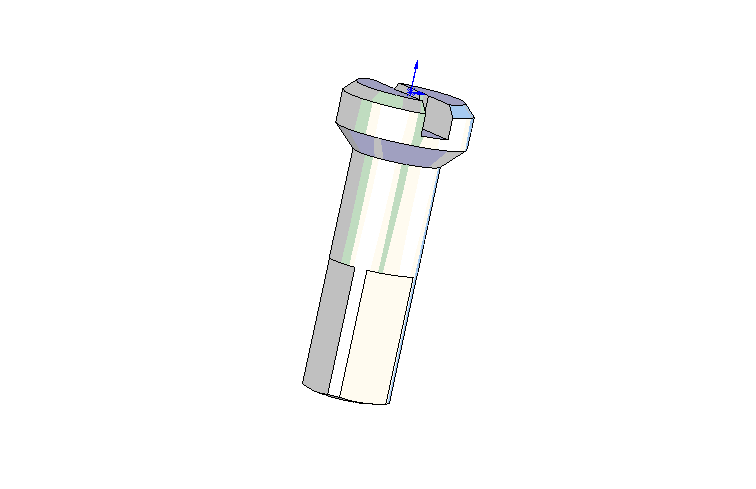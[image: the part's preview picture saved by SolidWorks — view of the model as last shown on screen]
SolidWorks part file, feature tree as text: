
SOLIDWORKS PART (.sldprt)
format: sldprt  version: not decoded by parser v0  size: 207,872 bytes
history: native  units: mm
features: plane x3, sketch x3, cut_extrude x2, material x1, revolve x1, chamfer x1 (+10 scaffold rows collapsed)
feature tree (21):
  scaffold x10  (default folders/planes/origin — collapsed)
  material  "Matériau <non spécifié>"
  plane  "Plan de face"
  plane  "Plan de dessus"
  plane  "Plan de droite"
  sketch  "Esquisse2"  dims[c1.D9=15.0mm c1.D1=1.6mm c1.D2=2.4mm c1.D3=6.0mm c1.D4=14.0mm c1.D5=2.0mm c1.D6=3.0mm c1.D7=6.0mm c1.D8=4.0mm c2.D3=6.0mm c2.D4=14.0mm]
  revolve  "Révolution1"  Angle=360deg
  chamfer  "Chanfrein1"  Distance=0.5mm Angle=45deg
  sketch  "Esquisse3"  dims[D1=1.4mm]
  cut_extrude  "Enlèv. mat.-Extru.1"  Depth=1.5mm
  sketch  "Esquisse4"  dims[D1=3.2mm]
  cut_extrude  "Enlèv. mat.-Extru.2"  [1 undecoded]
decode coverage: 6 of 7 modeling features carry decoded parameters
note: 1 parameter value undecoded
note: suppression state not decoded; provenance and decode notes live in map.json
